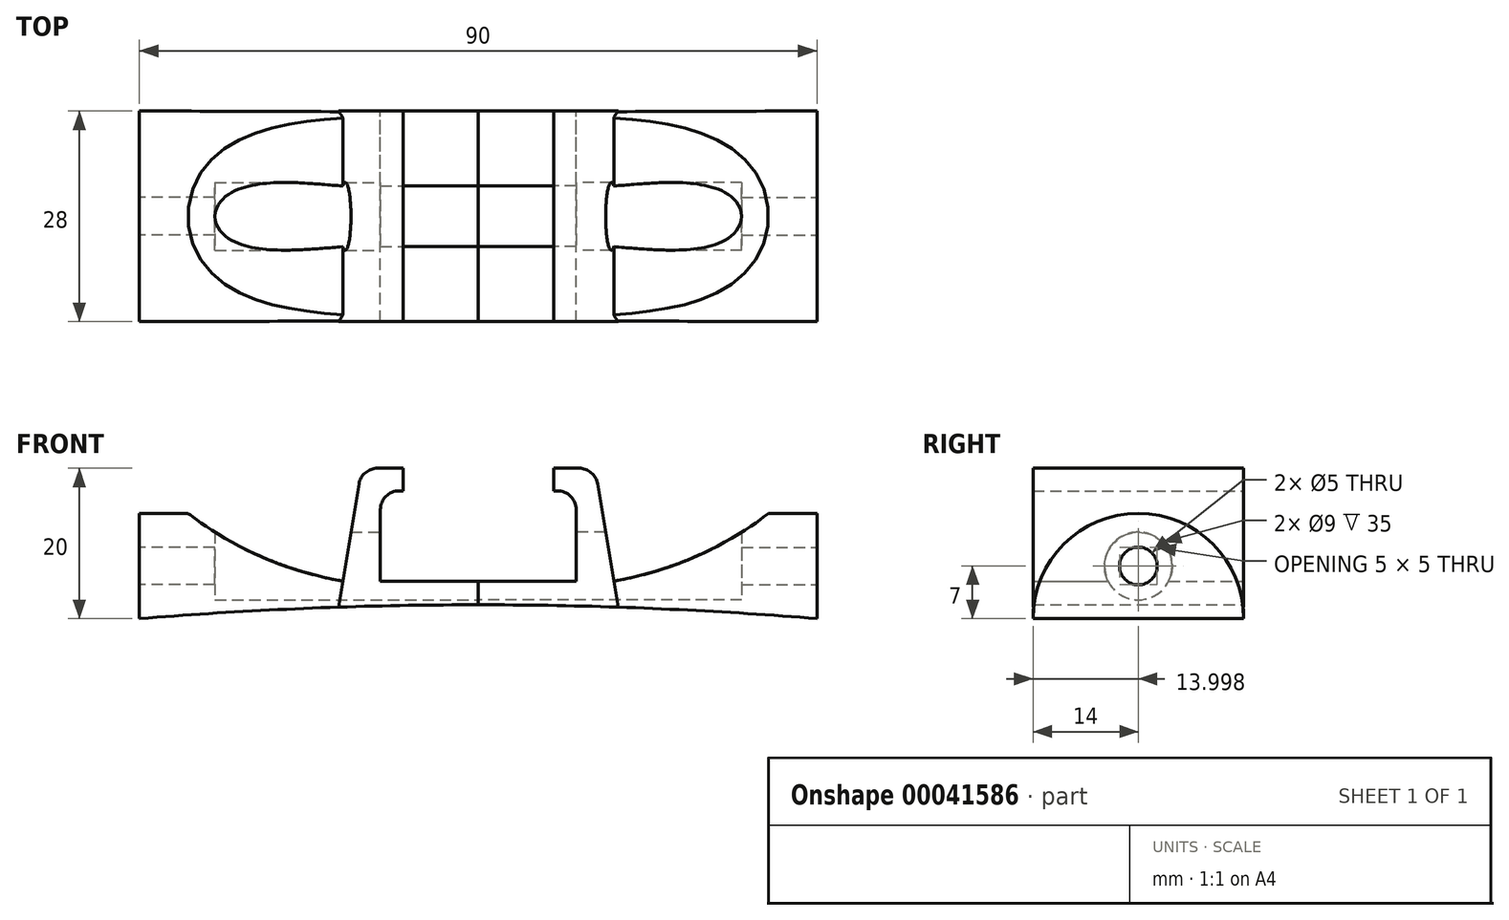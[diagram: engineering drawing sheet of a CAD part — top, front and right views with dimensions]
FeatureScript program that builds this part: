
annotation { "Feature Type Name" : "Feature", "Feature Type Description" : "" }
export const myFeature = defineFeature(function(context is Context, id is Id, definition is map)
    precondition{}
    {
        {
            var Q0;
            Q0=qCreatedBy(makeId("Front.planeOp"),FACE);
            var sketch = newSketch(context, id + "F0", { "sketchPlane" : qUnion([Q0])});
            skLineSegment(sketch, "E0.right", {"start": v(45, 0) * mm, "end": v(45, 20) * mm});
            skLineSegment(sketch, "E1.bottom", {"start": v(0, 5) * mm, "end": v(13, 5) * mm});
            skLineSegment(sketch, "E1.right", {"start": v(13, 5) * mm, "end": v(13, 17) * mm, "construction": true});
            skLineSegment(sketch, "E2", {"start": v(13, 14.5) * mm, "end": v(13, 5) * mm});
            skLineSegment(sketch, "E3.0", {"start": v(16, 17) * mm, "end": v(16, 5) * mm, "construction": true});
            skLineSegment(sketch, "E4.0", {"start": v(18, 17) * mm, "end": v(18, 5) * mm, "construction": true});
            skLineSegment(sketch, "E5", {"start": v(15.85, 17.91) * mm, "end": v(18, 5) * mm});
            skLineSegment(sketch, "E6.bottom", {"start": v(10.5, 17) * mm, "end": v(10, 17) * mm});
            skLineSegment(sketch, "E6.top", {"start": v(13.38, 20) * mm, "end": v(10, 20) * mm});
            skLineSegment(sketch, "E6.right", {"start": v(10, 17) * mm, "end": v(10, 20) * mm});
            skArc(sketch, "E7.filletArc", {"start": v(13, 14.5) * mm, "mid": v(12.27, 16.27) * mm, "end": v(10.5, 17) * mm});
            skPoint(sketch, "E8.visualSharp", {"position": v(15.5, 20) * mm});
            skArc(sketch, "E9", {"start": v(18, 5) * mm, "mid": v(32.78, 10.2) * mm, "end": v(45, 20) * mm});
            skArc(sketch, "E10", {"start": v(45, 0) * mm, "mid": v(22.52, 1.38) * mm, "end": v(0, 1.85) * mm});
            skArc(sketch, "E11.filletArc", {"start": v(15.85, 17.91) * mm, "mid": v(15, 19.4) * mm, "end": v(13.38, 20) * mm});
            skLineSegment(sketch, "E12", {"start": v(0, 5) * mm, "end": v(0, 1.85) * mm});
            skPoint(sketch, "E13.orphan", {"position": v(-45, 0) * mm});
            skSolve(sketch);
        }
        {
            var Q0;
            Q0 = qSketchRegion(id + "F0", true);
            extrude(context, id + "F1", {"entities" : qUnion([Q0]), "depth" : 28 * mm});
        }
        {
            var Q0;
            Q0=makeQuery(id+"F1.opExtrude","SWEPT_FACE",FACE,{"disambiguationData":[OSD([sQuery(id+"F0.wireOp",EDGE,"E0.right")])]});
            var sketch = newSketch(context, id + "F2", { "sketchPlane" : qUnion([Q0])});
            skArc(sketch, "E14", {"start": v(0, 0) * mm, "mid": v(-14, 14) * mm, "end": v(-28, 0) * mm});
            skLineSegment(sketch, "E15", {"start": v(-14, 0) * mm, "end": v(-14, 20) * mm, "construction": true});
            skLineSegment(sketch, "E16.0", {"start": v(-28, 7) * mm, "end": v(0, 7) * mm, "construction": true});
            skCircle(sketch, "E17", {"center": v(-14, 7) * mm, "radius": 2.5 * mm});
            skLineSegment(sketch, "E18", {"start": v(-28, 0) * mm, "end": v(-28, 20) * mm});
            skLineSegment(sketch, "E19", {"start": v(-28, 20) * mm, "end": v(0, 20) * mm});
            skLineSegment(sketch, "E20", {"start": v(0, 20) * mm, "end": v(0, 0) * mm});
            skSolve(sketch);
        }
        {
            var Q0;
            Q0=makeQuery(id+"F2.imprint","IMPRINT",FACE,{"disambiguationData":[TD([[makeQuery(id+"F2.imprint","IMPRINT",EDGE,{"derivedFrom":sQuery(id+"F2.wireOp",EDGE,"E14")}),-1.0]])]});
            var Q1;
            Q1=makeQuery(id+"F2.imprint","IMPRINT",FACE,{"disambiguationData":[TD([[makeQuery(id+"F2.imprint","IMPRINT",EDGE,{"derivedFrom":sQuery(id+"F2.wireOp",EDGE,"E17")}),1.0]])]});
            var Q2;
            Q2=makeQuery(id+"F1.opExtrude","SWEPT_FACE",FACE,{"disambiguationData":[OSD([sQuery(id+"F0.wireOp",EDGE,"E5")])]});
            extrude(context, id + "F3", {"entities" : qUnion([Q0, Q1]), "operationType" : NewBodyOperationType.REMOVE, "endBound" : BoundingType.UP_TO_SURFACE, "oppositeDirection" : true, "endBoundEntityFace" : qUnion([Q2]), "depth" : 25 * mm});
        }
        {
            var Q0;
            Q0=makeQuery(id+"F1.opExtrude","SWEPT_FACE",FACE,{"disambiguationData":[OSD([sQuery(id+"F0.wireOp",EDGE,"E12")])]});
            var sketch = newSketch(context, id + "F4", { "sketchPlane" : qUnion([Q0])});
            skLineSegment(sketch, "E21", {"start": v(14, -0.07) * mm, "end": v(14, 14.48) * mm, "construction": true});
            skPoint(sketch, "E21.endSnap0", {"position": v(14, 5) * mm});
            skLineSegment(sketch, "E22", {"start": v(0, 0) * mm, "end": v(28, 0) * mm});
            skLineSegment(sketch, "E23.0", {"start": v(0, 7) * mm, "end": v(28, 7) * mm, "construction": true});
            skCircle(sketch, "E24", {"center": v(14, 7) * mm, "radius": 4.5 * mm});
            skSolve(sketch);
        }
        {
            var Q0;
            Q0 = qSketchRegion(id + "F4", true);
            var Q1;
            Q1=makeQuery(id+"F1.opExtrude","SWEPT_FACE",FACE,{"disambiguationData":[OSD([sQuery(id+"F0.wireOp",EDGE,"E0.right")])]});
            extrude(context, id + "F5", {"entities" : qUnion([Q0]), "operationType" : NewBodyOperationType.REMOVE, "oppositeDirection" : true, "endBoundEntityFace" : qUnion([Q1]), "depth" : 35 * mm});
        }
        {
            var Q0;
            Q0=makeQuery(id+"F1.opExtrude","SWEPT_BODY",BODY,{"disambiguationData":[OSD([sQuery(id+"F0.wireOp",EDGE,"E0.right"),sQuery(id+"F0.wireOp",EDGE,"E1.bottom"),sQuery(id+"F0.wireOp",EDGE,"E2"),sQuery(id+"F0.wireOp",EDGE,"E5"),sQuery(id+"F0.wireOp",EDGE,"E6.bottom"),sQuery(id+"F0.wireOp",EDGE,"E6.top"),sQuery(id+"F0.wireOp",EDGE,"E6.right"),sQuery(id+"F0.wireOp",EDGE,"E7.filletArc"),sQuery(id+"F0.wireOp",EDGE,"E9"),sQuery(id+"F0.wireOp",EDGE,"E10"),sQuery(id+"F0.wireOp",EDGE,"E11.filletArc"),sQuery(id+"F0.wireOp",EDGE,"E12")])]});
            var Q1;
            Q1=makeQuery(id+"F1.opExtrude","SWEPT_FACE",FACE,{"disambiguationData":[OSD([sQuery(id+"F0.wireOp",EDGE,"E12")])]});
            mirror(context, id + "F6", {"entities" : qUnion([Q0]), "mirrorPlane" : qUnion([Q1])});
        }
    });
